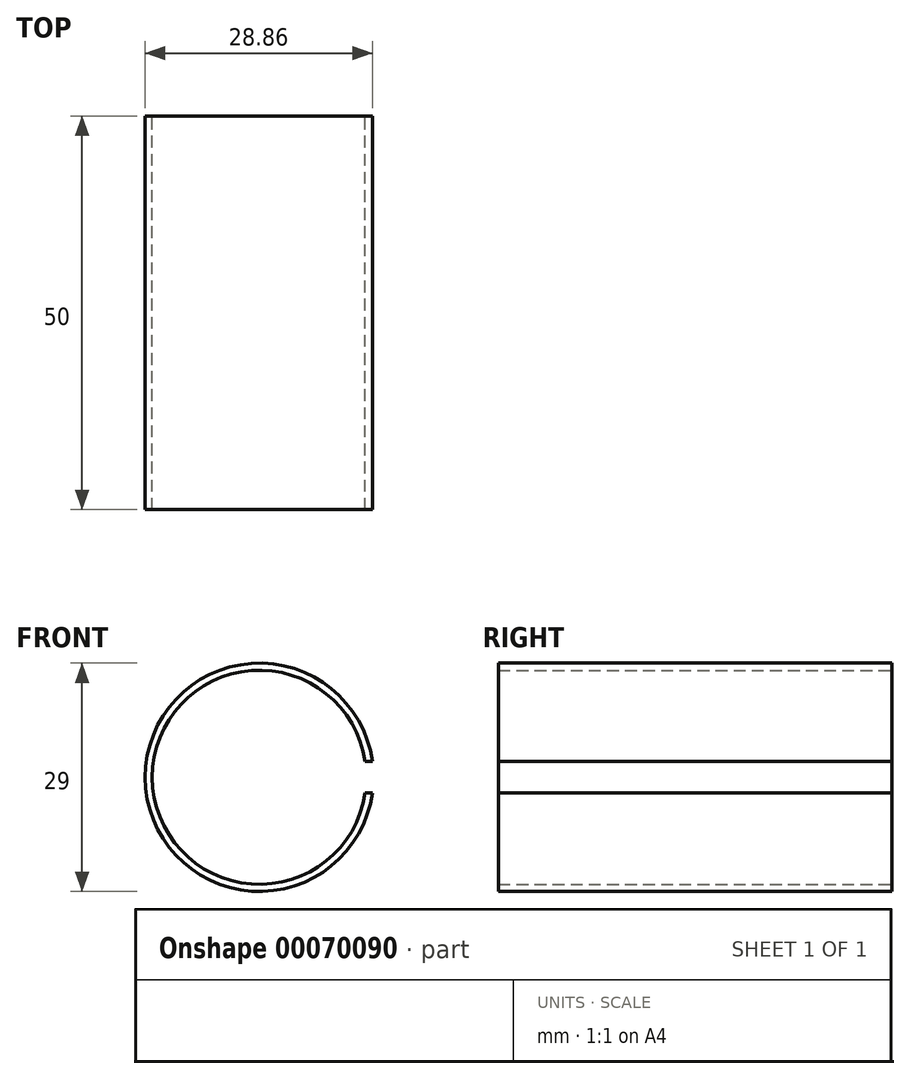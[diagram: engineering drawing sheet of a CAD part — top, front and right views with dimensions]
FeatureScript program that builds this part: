
annotation { "Feature Type Name" : "Feature", "Feature Type Description" : "" }
export const myFeature = defineFeature(function(context is Context, id is Id, definition is map)
    precondition{}
    {
        {
            var Q0;
            Q0=qCreatedBy(makeId("Front.planeOp"),FACE);
            var sketch = newSketch(context, id + "F0", { "sketchPlane" : qUnion([Q0])});
            skCircle(sketch, "E0", {"center": v(0, 0) * mm, "radius": 13.6 * mm});
            skCircle(sketch, "E1", {"center": v(0, 0) * mm, "radius": 14.5 * mm});
            skCircle(sketch, "E2", {"center": v(0, 0) * mm, "radius": 16.5 * mm});
            skLineSegment(sketch, "E3.bottom", {"start": v(19.98, -2) * mm, "end": v(7.98, -2) * mm});
            skLineSegment(sketch, "E3.top", {"start": v(19.98, 2) * mm, "end": v(7.98, 2) * mm});
            skLineSegment(sketch, "E3.left", {"start": v(19.98, -2) * mm, "end": v(19.98, 2) * mm});
            skLineSegment(sketch, "E3.right", {"start": v(7.98, -2) * mm, "end": v(7.98, 2) * mm});
            skLineSegment(sketch, "E4", {"start": v(7.98, 0) * mm, "end": v(19.98, 0) * mm, "construction": true});
            skSolve(sketch);
        }
        {
            var Q0;
            Q0=makeQuery(id+"F0.imprint","IMPRINT",FACE,{"disambiguationData":[TD([[makeQuery(id+"F0.imprint","IMPRINT",EDGE,{"derivedFrom":sQuery(id+"F0.wireOp",EDGE,"E0")}),-1.0]])]});
            extrude(context, id + "F1", {"entities" : qUnion([Q0]), "depth" : 50 * mm});
        }
        {
            var Q0;
            {var subQ5=sQuery(id+"F0.wireOp",EDGE,"E3.left");Q0=makeQuery(id+"F0.imprint","IMPRINT",FACE,{"disambiguationData":[TD([[makeQuery(id+"F0.imprint","IMPRINT",EDGE,{"derivedFrom":subQ5}),1.0]])]});}
            var Q1;
            {var subQ0=sQuery(id+"F0.wireOp",EDGE,"E3.bottom");var subQ1=sQuery(id+"F0.wireOp",EDGE,"E1");var subQ2=makeQuery(id+"F0.imprint","INTERSECT",VERTEX,{"derivedFrom":[subQ1,subQ0]});Q1=makeQuery(id+"F0.imprint","IMPRINT",FACE,{"disambiguationData":[TD([[makeQuery(id+"F0.imprint","IMPRINT",EDGE,{"disambiguationData":[TD([[subQ2,-1.0]])],"derivedFrom":subQ1}),-1.0]])]});}
            var Q2;
            {var subQ0=sQuery(id+"F0.wireOp",EDGE,"E3.bottom");var subQ1=sQuery(id+"F0.wireOp",EDGE,"E0");var subQ2=makeQuery(id+"F0.imprint","INTERSECT",VERTEX,{"derivedFrom":[subQ1,subQ0]});Q2=makeQuery(id+"F0.imprint","IMPRINT",FACE,{"disambiguationData":[TD([[makeQuery(id+"F0.imprint","IMPRINT",EDGE,{"disambiguationData":[TD([[subQ2,-1.0]])],"derivedFrom":subQ1}),-1.0]])]});}
            var Q3;
            {var subQ5=sQuery(id+"F0.wireOp",EDGE,"E3.right");Q3=makeQuery(id+"F0.imprint","IMPRINT",FACE,{"disambiguationData":[TD([[makeQuery(id+"F0.imprint","IMPRINT",EDGE,{"derivedFrom":subQ5}),-1.0]])]});}
            extrude(context, id + "F2", {"entities" : qUnion([Q0, Q1, Q2, Q3]), "operationType" : NewBodyOperationType.REMOVE, "depth" : 50 * mm});
        }
    });
